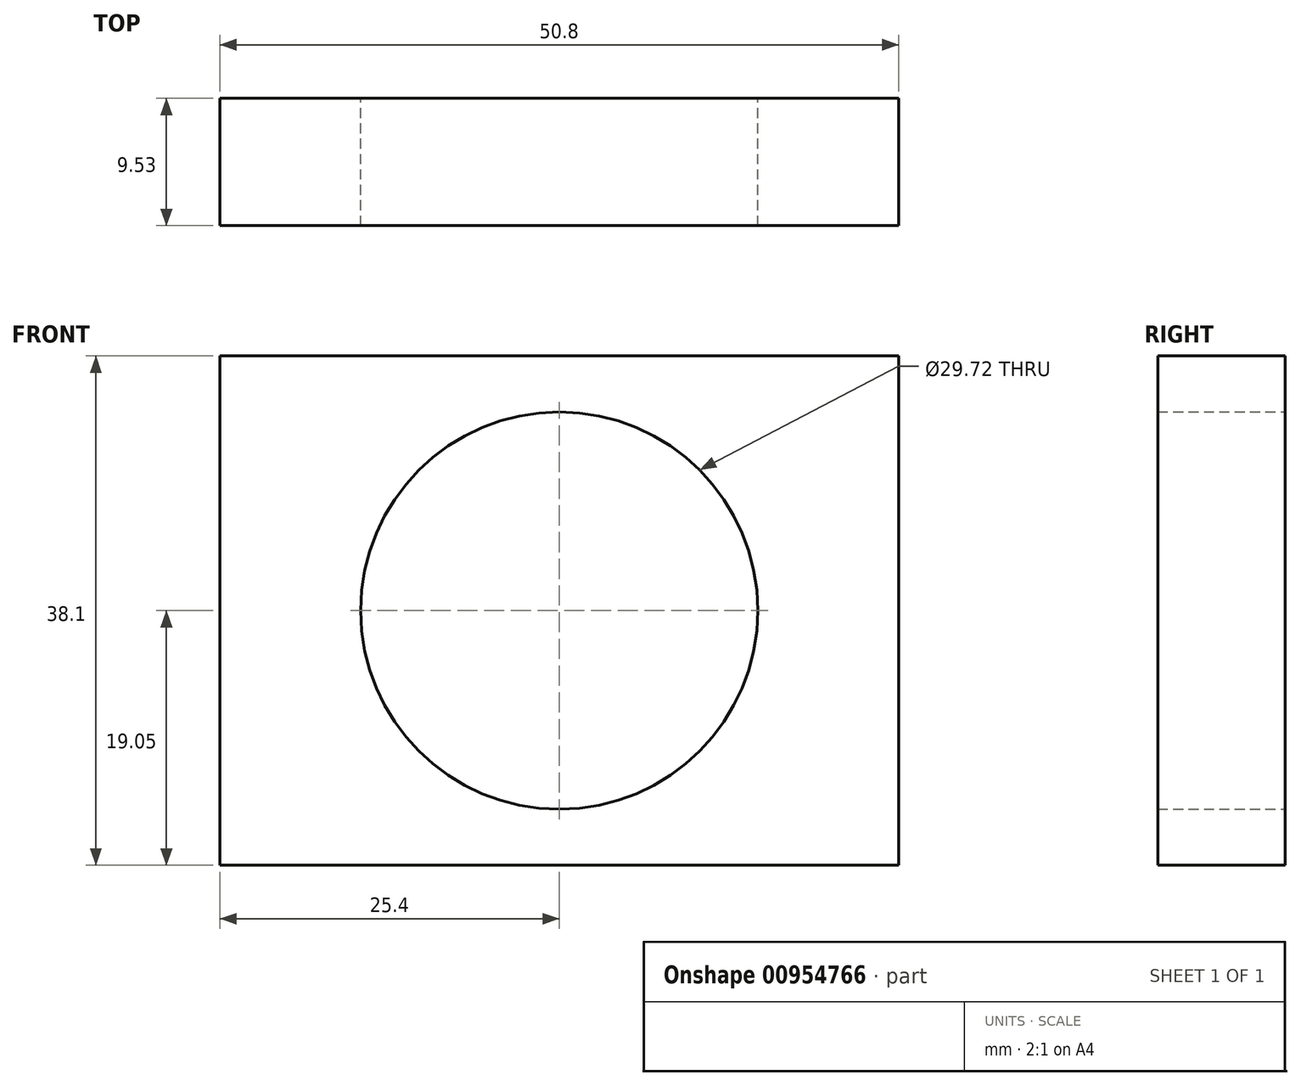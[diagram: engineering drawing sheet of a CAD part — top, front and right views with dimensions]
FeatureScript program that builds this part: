
annotation { "Feature Type Name" : "Feature", "Feature Type Description" : "" }
export const myFeature = defineFeature(function(context is Context, id is Id, definition is map)
    precondition{}
    {
        {
            var Q0;
            Q0=qCreatedBy(makeId("Front.planeOp"),FACE);
            var sketch = newSketch(context, id + "F0", { "sketchPlane" : qUnion([Q0])});
            skLineSegment(sketch, "E0.bottom", {"start": v(-25.4, -19.05) * mm, "end": v(25.4, -19.05) * mm});
            skLineSegment(sketch, "E0.top", {"start": v(-25.4, 19.05) * mm, "end": v(25.4, 19.05) * mm});
            skLineSegment(sketch, "E0.left", {"start": v(-25.4, -19.05) * mm, "end": v(-25.4, 19.05) * mm});
            skLineSegment(sketch, "E0.right", {"start": v(25.4, -19.05) * mm, "end": v(25.4, 19.05) * mm});
            skCircle(sketch, "E1", {"center": v(0, 0) * mm, "radius": 14.86 * mm});
            skSolve(sketch);
        }
        {
            var Q0;
            Q0=makeQuery(id+"F0.imprint","IMPRINT",FACE,{"disambiguationData":[TD([[makeQuery(id+"F0.imprint","IMPRINT",EDGE,{"derivedFrom":sQuery(id+"F0.wireOp",EDGE,"E0.bottom")}),1.0]])]});
            extrude(context, id + "F1", {"entities" : qUnion([Q0]), "depth" : 9.52 * mm, "offsetDistance" : 25.4 * mm});
        }
    });
